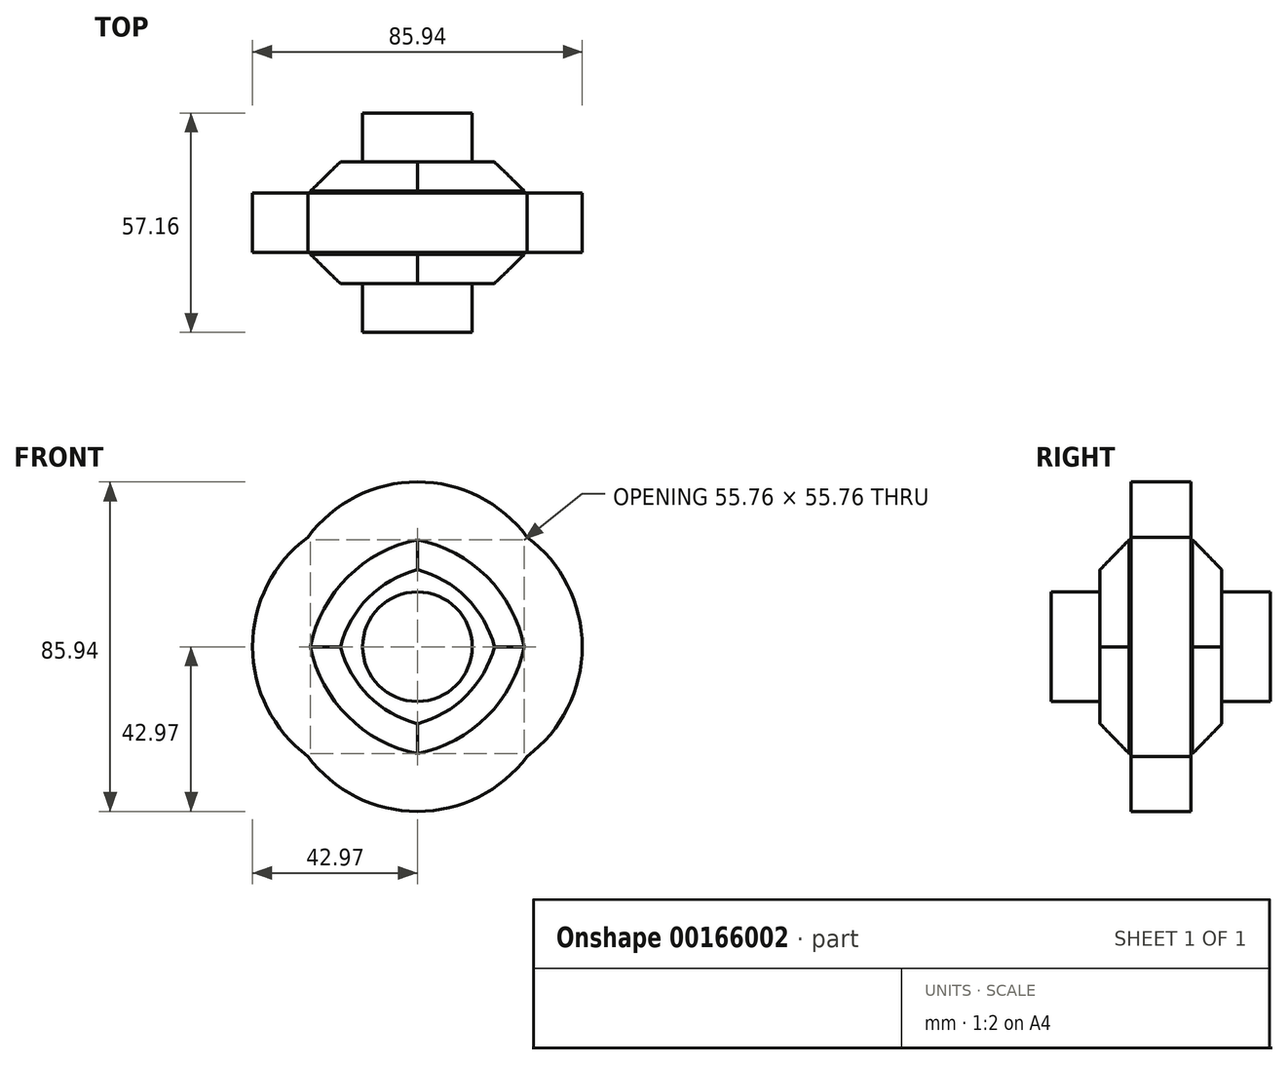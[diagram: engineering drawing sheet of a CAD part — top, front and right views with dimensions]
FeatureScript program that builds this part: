
annotation { "Feature Type Name" : "Feature", "Feature Type Description" : "" }
export const myFeature = defineFeature(function(context is Context, id is Id, definition is map)
    precondition{}
    {
        {
            var Q0;
            Q0=qCreatedBy(makeId("Front.planeOp"),FACE);
            var sketch = newSketch(context, id + "F0", { "sketchPlane" : qUnion([Q0])});
            skPoint(sketch, "E0.middle", {"position": v(0, 0) * mm});
            skArc(sketch, "E1", {"start": v(-28.58, 28.57) * mm, "mid": v(-42.97, 0) * mm, "end": v(-28.58, -28.58) * mm});
            skArc(sketch, "E2", {"start": v(28.58, 28.58) * mm, "mid": v(0, 42.97) * mm, "end": v(-28.57, 28.58) * mm});
            skArc(sketch, "E3", {"start": v(28.58, -28.58) * mm, "mid": v(42.97, 0) * mm, "end": v(28.58, 28.58) * mm});
            skArc(sketch, "E4", {"start": v(-28.58, -28.58) * mm, "mid": v(0, -42.97) * mm, "end": v(28.57, -28.58) * mm});
            skLineSegment(sketch, "E5", {"start": v(0, -27.88) * mm, "end": v(0, 27.88) * mm});
            skLineSegment(sketch, "E6", {"start": v(-27.88, 0) * mm, "end": v(27.88, 0) * mm});
            skCircle(sketch, "E7", {"center": v(0, 0) * mm, "radius": 14.29 * mm});
            skPoint(sketch, "E8.visualSharp", {"position": v(28.57, -28.58) * mm});
            skArc(sketch, "E8.filletArc", {"start": v(0, -27.88) * mm, "mid": v(18.16, -18.16) * mm, "end": v(27.88, 0) * mm});
            skPoint(sketch, "E9.visualSharp", {"position": v(-28.58, -28.58) * mm});
            skArc(sketch, "E9.filletArc", {"start": v(-27.88, 0) * mm, "mid": v(-18.16, -18.16) * mm, "end": v(0, -27.88) * mm});
            skPoint(sketch, "E10.visualSharp", {"position": v(-28.57, 28.58) * mm});
            skArc(sketch, "E10.filletArc", {"start": v(0, 27.88) * mm, "mid": v(-18.16, 18.16) * mm, "end": v(-27.88, 0) * mm});
            skPoint(sketch, "E11.visualSharp", {"position": v(28.58, 28.58) * mm});
            skArc(sketch, "E11.filletArc", {"start": v(27.88, 0) * mm, "mid": v(18.16, 18.16) * mm, "end": v(0, 27.88) * mm});
            skPoint(sketch, "E12.orphan", {"position": v(-42.97, 0) * mm});
            skPoint(sketch, "E13.orphan", {"position": v(0, -42.97) * mm});
            skPoint(sketch, "E14.orphan", {"position": v(0, 42.97) * mm});
            skPoint(sketch, "E15.orphan", {"position": v(42.97, 0) * mm});
            skSolve(sketch);
        }
        {
            var Q0;
            {var subQ0=sQuery(id+"F0.wireOp",EDGE,"E6");var subQ1=sQuery(id+"F0.wireOp",EDGE,"E5");var subQ2=makeQuery(id+"F0.imprint","INTERSECT",VERTEX,{"derivedFrom":[subQ1,subQ0]});Q0=makeQuery(id+"F0.imprint","IMPRINT",FACE,{"disambiguationData":[TD([[makeQuery(id+"F0.imprint","IMPRINT",EDGE,{"disambiguationData":[TD([[subQ2,-1.0]])],"derivedFrom":subQ1}),1.0]])]});}
            var Q1;
            {var subQ0=sQuery(id+"F0.wireOp",EDGE,"E7");var subQ1=sQuery(id+"F0.wireOp",EDGE,"E5");var subQ2=makeQuery(id+"F0.imprint","INTERSECT",VERTEX,{"disambiguationData":[OD(0.0)],"derivedFrom":[subQ1,subQ0]});Q1=makeQuery(id+"F0.imprint","IMPRINT",FACE,{"disambiguationData":[TD([[makeQuery(id+"F0.imprint","IMPRINT",EDGE,{"disambiguationData":[TD([[subQ2,-1.0]])],"derivedFrom":subQ1}),1.0]])]});}
            var Q2;
            {var subQ0=sQuery(id+"F0.wireOp",EDGE,"E7");var subQ1=sQuery(id+"F0.wireOp",EDGE,"E5");var subQ2=makeQuery(id+"F0.imprint","INTERSECT",VERTEX,{"disambiguationData":[OD(0.0)],"derivedFrom":[subQ1,subQ0]});Q2=makeQuery(id+"F0.imprint","IMPRINT",FACE,{"disambiguationData":[TD([[makeQuery(id+"F0.imprint","IMPRINT",EDGE,{"disambiguationData":[TD([[subQ2,-1.0]])],"derivedFrom":subQ1}),-1.0]])]});}
            var Q3;
            {var subQ0=sQuery(id+"F0.wireOp",EDGE,"E6");var subQ1=sQuery(id+"F0.wireOp",EDGE,"E5");var subQ2=makeQuery(id+"F0.imprint","INTERSECT",VERTEX,{"derivedFrom":[subQ1,subQ0]});Q3=makeQuery(id+"F0.imprint","IMPRINT",FACE,{"disambiguationData":[TD([[makeQuery(id+"F0.imprint","IMPRINT",EDGE,{"disambiguationData":[TD([[subQ2,-1.0]])],"derivedFrom":subQ1}),-1.0]])]});}
            extrude(context, id + "F1", {"entities" : qUnion([Q0, Q1, Q2, Q3]), "endBound" : BoundingType.SYMMETRIC, "oppositeDirection" : true, "depth" : 57.15 * mm});
        }
        {
            var Q0;
            {var subQ0=sQuery(id+"F0.wireOp",EDGE,"E7");var subQ1=sQuery(id+"F0.wireOp",EDGE,"E5");var subQ2=makeQuery(id+"F0.imprint","INTERSECT",VERTEX,{"disambiguationData":[OD(1.0)],"derivedFrom":[subQ1,subQ0]});Q0=makeQuery(id+"F0.imprint","IMPRINT",FACE,{"disambiguationData":[TD([[makeQuery(id+"F0.imprint","IMPRINT",EDGE,{"disambiguationData":[TD([[subQ2,-1.0]])],"derivedFrom":subQ0}),-1.0]])]});}
            var Q1;
            {var subQ0=sQuery(id+"F0.wireOp",EDGE,"E7");var subQ1=sQuery(id+"F0.wireOp",EDGE,"E5");var subQ2=makeQuery(id+"F0.imprint","INTERSECT",VERTEX,{"disambiguationData":[OD(1.0)],"derivedFrom":[subQ1,subQ0]});Q1=makeQuery(id+"F0.imprint","IMPRINT",FACE,{"disambiguationData":[TD([[makeQuery(id+"F0.imprint","IMPRINT",EDGE,{"disambiguationData":[TD([[subQ2,1.0]])],"derivedFrom":subQ0}),-1.0]])]});}
            var Q2;
            {var subQ0=sQuery(id+"F0.wireOp",EDGE,"E7");var subQ1=sQuery(id+"F0.wireOp",EDGE,"E5");var subQ2=makeQuery(id+"F0.imprint","INTERSECT",VERTEX,{"disambiguationData":[OD(0.0)],"derivedFrom":[subQ1,subQ0]});Q2=makeQuery(id+"F0.imprint","IMPRINT",FACE,{"disambiguationData":[TD([[makeQuery(id+"F0.imprint","IMPRINT",EDGE,{"disambiguationData":[TD([[subQ2,-1.0]])],"derivedFrom":subQ0}),-1.0]])]});}
            var Q3;
            {var subQ0=sQuery(id+"F0.wireOp",EDGE,"E7");var subQ1=sQuery(id+"F0.wireOp",EDGE,"E5");var subQ2=makeQuery(id+"F0.imprint","INTERSECT",VERTEX,{"disambiguationData":[OD(0.0)],"derivedFrom":[subQ1,subQ0]});Q3=makeQuery(id+"F0.imprint","IMPRINT",FACE,{"disambiguationData":[TD([[makeQuery(id+"F0.imprint","IMPRINT",EDGE,{"disambiguationData":[TD([[subQ2,1.0]])],"derivedFrom":subQ0}),-1.0]])]});}
            extrude(context, id + "F2", {"entities" : qUnion([Q0, Q1, Q2, Q3]), "operationType" : NewBodyOperationType.ADD, "endBound" : BoundingType.SYMMETRIC, "depth" : 31.75 * mm});
        }
        {
            var Q0;
            Q0 = qSketchRegion(id + "F0", true);
            extrude(context, id + "F3", {"entities" : qUnion([Q0]), "operationType" : NewBodyOperationType.ADD, "endBound" : BoundingType.SYMMETRIC, "depth" : 15.56 * mm});
        }
        {
            var Q0;
            Q0=makeQuery(id+"F2.opExtrude","CAP_EDGE",EDGE,{"disambiguationData":[OSD([sQuery(id+"F0.wireOp",EDGE,"E9.filletArc")])],"isStart":false});
            var Q1;
            Q1=makeQuery(id+"F2.opExtrude","CAP_EDGE",EDGE,{"disambiguationData":[OSD([sQuery(id+"F0.wireOp",EDGE,"E10.filletArc")])],"isStart":false});
            var Q2;
            Q2=makeQuery(id+"F2.opExtrude","CAP_EDGE",EDGE,{"disambiguationData":[OSD([sQuery(id+"F0.wireOp",EDGE,"E8.filletArc")])],"isStart":false});
            var Q3;
            Q3=makeQuery(id+"F2.opExtrude","CAP_EDGE",EDGE,{"disambiguationData":[OSD([sQuery(id+"F0.wireOp",EDGE,"E11.filletArc")])],"isStart":false});
            var Q4;
            Q4=makeQuery(id+"F2.opExtrude","CAP_EDGE",EDGE,{"disambiguationData":[OSD([sQuery(id+"F0.wireOp",EDGE,"E10.filletArc")])],"isStart":true});
            var Q5;
            Q5=makeQuery(id+"F2.opExtrude","CAP_EDGE",EDGE,{"disambiguationData":[OSD([sQuery(id+"F0.wireOp",EDGE,"E9.filletArc")])],"isStart":true});
            var Q6;
            Q6=makeQuery(id+"F2.opExtrude","CAP_EDGE",EDGE,{"disambiguationData":[OSD([sQuery(id+"F0.wireOp",EDGE,"E8.filletArc")])],"isStart":true});
            var Q7;
            Q7=makeQuery(id+"F2.opExtrude","CAP_EDGE",EDGE,{"disambiguationData":[OSD([sQuery(id+"F0.wireOp",EDGE,"E11.filletArc")])],"isStart":true});
            chamfer(context, id + "F4", {"entities" : qUnion([Q0, Q1, Q2, Q3, Q4, Q5, Q6, Q7]), "width" : 7.62 * mm, "tangentPropagation" : true});
        }
    });
